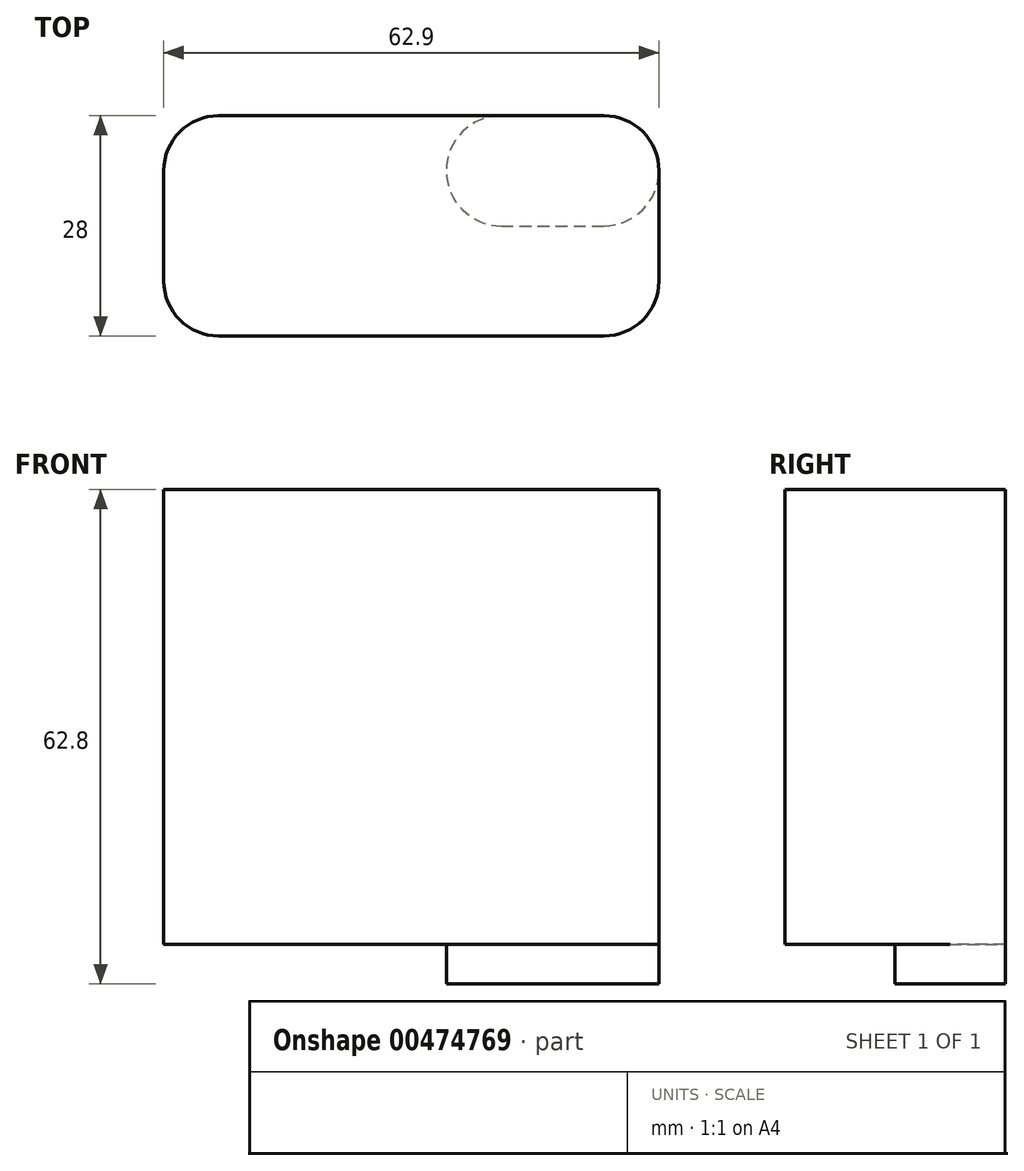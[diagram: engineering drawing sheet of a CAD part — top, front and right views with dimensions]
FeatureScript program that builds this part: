
annotation { "Feature Type Name" : "Feature", "Feature Type Description" : "" }
export const myFeature = defineFeature(function(context is Context, id is Id, definition is map)
    precondition{}
    {
        {
            var Q0;
            Q0=qCreatedBy(makeId("Front.planeOp"),FACE);
            var sketch = newSketch(context, id + "F0", { "sketchPlane" : qUnion([Q0])});
            skLineSegment(sketch, "E0.bottom", {"start": v(0, 0) * mm, "end": v(62.9, 0) * mm});
            skLineSegment(sketch, "E0.top", {"start": v(0, 57.8) * mm, "end": v(62.9, 57.8) * mm});
            skLineSegment(sketch, "E0.left", {"start": v(0, 0) * mm, "end": v(0, 57.8) * mm});
            skLineSegment(sketch, "E0.right", {"start": v(62.9, 0) * mm, "end": v(62.9, 57.8) * mm});
            skSolve(sketch);
        }
        {
            var Q0;
            Q0 = qSketchRegion(id + "F0", true);
            extrude(context, id + "F1", {"entities" : qUnion([Q0]), "depth" : 28 * mm});
        }
        {
            var Q0;
            Q0=makeQuery(id+"F1.opExtrude","CAP_EDGE",EDGE,{"disambiguationData":[OSD([sQuery(id+"F0.wireOp",EDGE,"E0.left")])],"isStart":false});
            var Q1;
            Q1=makeQuery(id+"F1.opExtrude","CAP_EDGE",EDGE,{"disambiguationData":[OSD([sQuery(id+"F0.wireOp",EDGE,"E0.left")])],"isStart":true});
            var Q2;
            Q2=makeQuery(id+"F1.opExtrude","CAP_EDGE",EDGE,{"disambiguationData":[OSD([sQuery(id+"F0.wireOp",EDGE,"E0.right")])],"isStart":false});
            var Q3;
            Q3=makeQuery(id+"F1.opExtrude","CAP_EDGE",EDGE,{"disambiguationData":[OSD([sQuery(id+"F0.wireOp",EDGE,"E0.right")])],"isStart":true});
            fillet(context, id + "F2", {"entities" : qUnion([Q0, Q1, Q2, Q3]), "radius" : 7 * mm, "tangentPropagation" : true, "allowEdgeOverflow" : false});
        }
        {
            var Q0;
            Q0=makeQuery(id+"F1.opExtrude","SWEPT_FACE",FACE,{"disambiguationData":[OSD([sQuery(id+"F0.wireOp",EDGE,"E0.bottom")])]});
            var sketch = newSketch(context, id + "F3", { "sketchPlane" : qUnion([Q0])});
            skLineSegment(sketch, "E1", {"start": v(42.9, 14) * mm, "end": v(55.9, 14) * mm});
            skLineSegment(sketch, "E2", {"start": v(42.9, 0) * mm, "end": v(55.9, 0) * mm});
            skArc(sketch, "E3", {"start": v(55.9, 0) * mm, "mid": v(62.9, 7) * mm, "end": v(55.9, 14) * mm});
            skArc(sketch, "E4", {"start": v(42.9, 14) * mm, "mid": v(35.9, 7) * mm, "end": v(42.9, 0) * mm});
            skSolve(sketch);
        }
        {
            var Q0;
            Q0 = qSketchRegion(id + "F3", true);
            extrude(context, id + "F4", {"entities" : qUnion([Q0]), "operationType" : NewBodyOperationType.ADD, "depth" : 5 * mm});
        }
    });
